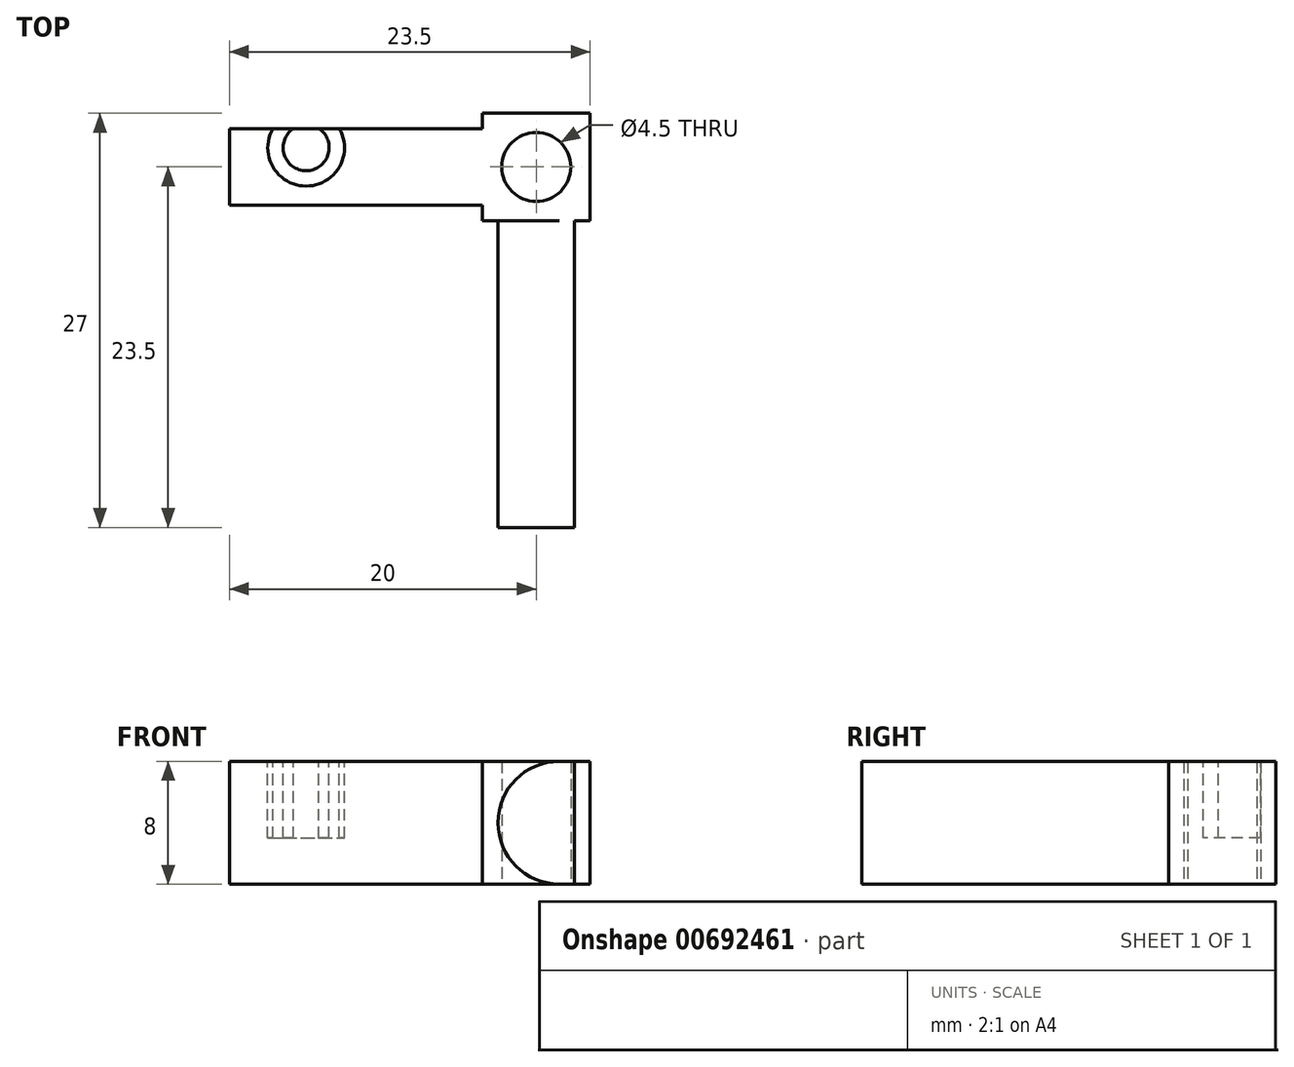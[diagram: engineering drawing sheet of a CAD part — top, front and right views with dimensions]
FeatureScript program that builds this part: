
annotation { "Feature Type Name" : "Feature", "Feature Type Description" : "" }
export const myFeature = defineFeature(function(context is Context, id is Id, definition is map)
    precondition{}
    {
        {
            var Q0;
            Q0=qCreatedBy(makeId("Top.planeOp"),FACE);
            var sketch = newSketch(context, id + "F0", { "sketchPlane" : qUnion([Q0])});
            skLineSegment(sketch, "E0.bottom", {"start": v(2.5, -10) * mm, "end": v(-2.5, -10) * mm});
            skLineSegment(sketch, "E0.top", {"start": v(2.5, 10) * mm, "end": v(-2.5, 10) * mm});
            skLineSegment(sketch, "E0.left", {"start": v(2.5, -10) * mm, "end": v(2.5, 10) * mm});
            skLineSegment(sketch, "E0.right", {"start": v(-2.5, -10) * mm, "end": v(-2.5, 10) * mm});
            skPoint(sketch, "E0.middle", {"position": v(0, 0) * mm});
            skLineSegment(sketch, "E1", {"start": v(-2.5, 10) * mm, "end": v(-3.5, 10) * mm});
            skLineSegment(sketch, "E2", {"start": v(2.5, 10) * mm, "end": v(3.5, 10) * mm});
            skLineSegment(sketch, "E3", {"start": v(3.5, 10) * mm, "end": v(3.5, 17) * mm});
            skLineSegment(sketch, "E4", {"start": v(3.5, 17) * mm, "end": v(-3.5, 17) * mm});
            skLineSegment(sketch, "E5", {"start": v(-3.5, 17) * mm, "end": v(-3.5, 10) * mm});
            skPoint(sketch, "E6", {"position": v(0, 13.5) * mm});
            skPoint(sketch, "E6.positionSnap0", {"position": v(3.5, 13.5) * mm});
            skPoint(sketch, "E6.positionSnap1", {"position": v(0, 10) * mm});
            skCircle(sketch, "E7", {"center": v(0, 13.5) * mm, "radius": 2.25 * mm});
            skLineSegment(sketch, "E8", {"start": v(-3.5, 10) * mm, "end": v(-3.5, 11) * mm});
            skLineSegment(sketch, "E9", {"start": v(-3.5, 11) * mm, "end": v(-20, 11) * mm});
            skLineSegment(sketch, "E10", {"start": v(-20, 11) * mm, "end": v(-20, 16) * mm});
            skLineSegment(sketch, "E11", {"start": v(-20, 16) * mm, "end": v(-3.5, 16) * mm});
            skSolve(sketch);
        }
        {
            var Q0;
            Q0=makeQuery(id+"F0.imprint","IMPRINT",FACE,{"disambiguationData":[TD([[makeQuery(id+"F0.imprint","IMPRINT",EDGE,{"derivedFrom":sQuery(id+"F0.wireOp",EDGE,"E0.bottom")}),-1.0]])]});
            var Q1;
            Q1=makeQuery(id+"F0.imprint","IMPRINT",FACE,{"disambiguationData":[TD([[makeQuery(id+"F0.imprint","IMPRINT",EDGE,{"derivedFrom":sQuery(id+"F0.wireOp",EDGE,"E0.top")}),-1.0]])]});
            var Q2;
            {var subQ0=sQuery(id+"F0.wireOp",EDGE,"fkc1CDvE-MzZ7-92Op-FZaX-3nJgZqbVmx0M");Q2=makeQuery(id+"F0.imprint","IMPRINT",FACE,{"disambiguationData":[TD([[makeQuery(id+"F0.imprint","IMPRINT",EDGE,{"derivedFrom":subQ0}),-1.0]])]});}
            var Q3;
            {var subQ0=sQuery(id+"F0.wireOp",EDGE,"E9");Q3=makeQuery(id+"F0.imprint","IMPRINT",FACE,{"disambiguationData":[TD([[makeQuery(id+"F0.imprint","IMPRINT",EDGE,{"derivedFrom":subQ0}),-1.0]])]});}
            extrude(context, id + "F1", {"entities" : qUnion([Q0, Q1, Q2, Q3]), "depth" : 8 * mm, "offsetDistance" : 25 * mm});
        }
        {
            var Q0;
            Q0=makeQuery(id+"F1.opExtrude","CAP_EDGE",EDGE,{"disambiguationData":[OSD([sQuery(id+"F0.wireOp",EDGE,"E0.right")])],"isStart":false});
            var Q1;
            Q1=makeQuery(id+"F1.opExtrude","CAP_EDGE",EDGE,{"disambiguationData":[OSD([sQuery(id+"F0.wireOp",EDGE,"E0.right")])],"isStart":true});
            fillet(context, id + "F2", {"entities" : qUnion([Q0, Q1]), "radius" : 4 * mm, "tangentPropagation" : true, "allowEdgeOverflow" : false});
        }
        {
            var Q0;
            Q0=makeQuery(id+"F1.opExtrude","CAP_FACE",FACE,{"disambiguationData":[OSD([sQuery(id+"F0.wireOp",EDGE,"E0.bottom"),sQuery(id+"F0.wireOp",EDGE,"E0.left"),sQuery(id+"F0.wireOp",EDGE,"E0.right"),sQuery(id+"F0.wireOp",EDGE,"E1"),sQuery(id+"F0.wireOp",EDGE,"E2"),sQuery(id+"F0.wireOp",EDGE,"E3"),sQuery(id+"F0.wireOp",EDGE,"E4"),sQuery(id+"F0.wireOp",EDGE,"E5"),sQuery(id+"F0.wireOp",EDGE,"E7"),sQuery(id+"F0.wireOp",EDGE,"E8"),sQuery(id+"F0.wireOp",EDGE,"E9"),sQuery(id+"F0.wireOp",EDGE,"E10"),sQuery(id+"F0.wireOp",EDGE,"E11")])],"isStart":false});
            var sketch = newSketch(context, id + "F3", { "sketchPlane" : qUnion([Q0])});
            skLineSegment(sketch, "E12", {"start": v(0, 13.5) * mm, "end": v(-15, 13.5) * mm, "construction": true});
            skLineSegment(sketch, "E13", {"start": v(-15, 13.5) * mm, "end": v(-15, 16) * mm, "construction": true});
            skCircle(sketch, "E14", {"center": v(-15, 14.75) * mm, "radius": 1.5 * mm});
            skCircle(sketch, "E15", {"center": v(-15, 14.75) * mm, "radius": 2.5 * mm});
            skSolve(sketch);
        }
        {
            var Q0;
            Q0=makeQuery(id+"F3.imprint","IMPRINT",FACE,{"disambiguationData":[TD([[makeQuery(id+"F3.imprint","IMPRINT",EDGE,{"derivedFrom":sQuery(id+"F3.wireOp",EDGE,"E14")}),-1.0]])]});
            extrude(context, id + "F4", {"entities" : qUnion([Q0]), "operationType" : NewBodyOperationType.REMOVE, "oppositeDirection" : true, "depth" : 5 * mm, "offsetDistance" : 25 * mm});
        }
    });
